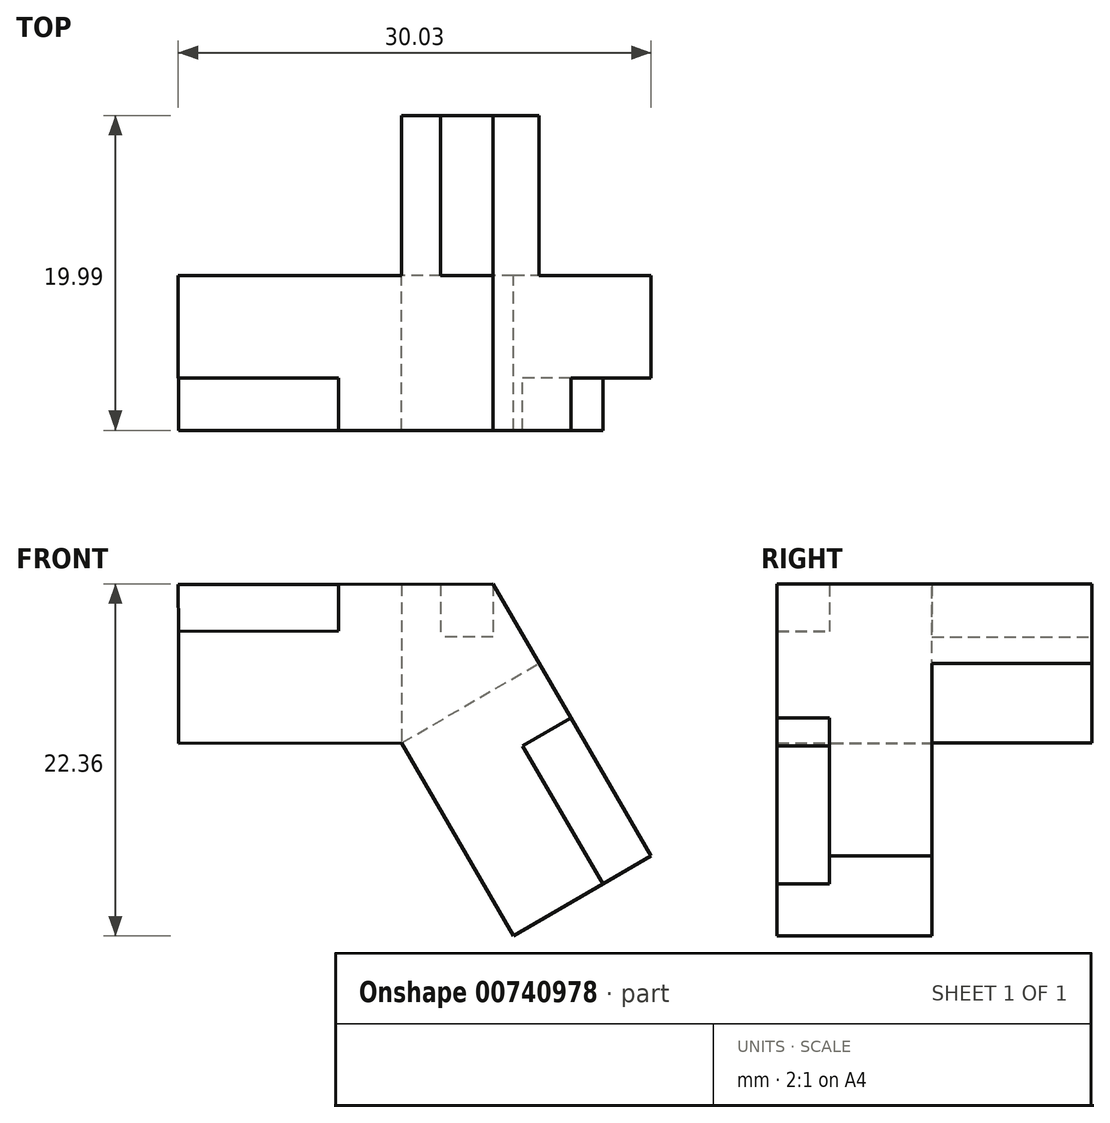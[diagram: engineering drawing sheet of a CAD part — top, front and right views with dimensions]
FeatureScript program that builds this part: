
annotation { "Feature Type Name" : "Feature", "Feature Type Description" : "" }
export const myFeature = defineFeature(function(context is Context, id is Id, definition is map)
    precondition{}
    {
        {
            var Q0;
            Q0=qCreatedBy(makeId("Front.planeOp"),FACE);
            var sketch = newSketch(context, id + "F0", { "sketchPlane" : qUnion([Q0])});
            skLineSegment(sketch, "E0.0", {"start": v(14.19, 24.71) * mm, "end": v(21.3, 12.46) * mm});
            skLineSegment(sketch, "E0.5", {"start": v(0.02, 24.68) * mm, "end": v(14.19, 24.71) * mm});
            skPoint(sketch, "E0.0.midPoint", {"position": v(21.3, 12.46) * mm});
            skLineSegment(sketch, "E1.0", {"start": v(19.99, 34.82) * mm, "end": v(30.03, 17.53) * mm});
            skLineSegment(sketch, "E1.5", {"start": v(0, 34.77) * mm, "end": v(19.99, 34.82) * mm});
            skPoint(sketch, "E1.0.midPoint", {"position": v(30.03, 17.53) * mm});
            skLineSegment(sketch, "E2", {"start": v(0, 34.77) * mm, "end": v(0.02, 24.68) * mm});
            skLineSegment(sketch, "E3", {"start": v(21.3, 12.46) * mm, "end": v(30.03, 17.53) * mm});
            skPoint(sketch, "E4.orphan", {"position": v(28.41, 0.21) * mm});
            skPoint(sketch, "E5.orphan", {"position": v(40.06, 0.24) * mm});
            skSolve(sketch);
        }
        {
            var Q0;
            Q0 = qSketchRegion(id + "F0", true);
            extrude(context, id + "F1", {"entities" : qUnion([Q0]), "depth" : 19.99 * mm, "offsetDistance" : 25.4 * mm});
        }
        {
            var Q0;
            Q0=makeQuery(id+"F1.opExtrude","CAP_FACE",FACE,{"disambiguationData":[OSD([sQuery(id+"F0.wireOp",EDGE,"E0.0"),sQuery(id+"F0.wireOp",EDGE,"E0.5"),sQuery(id+"F0.wireOp",EDGE,"E1.0"),sQuery(id+"F0.wireOp",EDGE,"E1.5"),sQuery(id+"F0.wireOp",EDGE,"E2"),sQuery(id+"F0.wireOp",EDGE,"E3")])],"isStart":true});
            var sketch = newSketch(context, id + "F2", { "sketchPlane" : qUnion([Q0])});
            skLineSegment(sketch, "E6.bottom", {"start": v(-19.99, 34.82) * mm, "end": v(-16.66, 34.82) * mm});
            skLineSegment(sketch, "E6.top", {"start": v(-19.99, 31.46) * mm, "end": v(-16.66, 31.46) * mm});
            skLineSegment(sketch, "E6.left", {"start": v(-19.99, 34.82) * mm, "end": v(-19.99, 31.46) * mm});
            skLineSegment(sketch, "E6.right", {"start": v(-16.66, 34.82) * mm, "end": v(-16.66, 31.46) * mm});
            skSolve(sketch);
        }
        {
            var Q0;
            Q0 = qSketchRegion(id + "F2", true);
            extrude(context, id + "F3", {"entities" : qUnion([Q0]), "operationType" : NewBodyOperationType.REMOVE, "oppositeDirection" : true, "depth" : 10.16 * mm, "offsetDistance" : 25.4 * mm});
        }
        {
            var Q0;
            Q0=makeQuery(id+"F1.opExtrude","SWEPT_FACE",FACE,{"disambiguationData":[OSD([sQuery(id+"F0.wireOp",EDGE,"E2")])]});
            var sketch = newSketch(context, id + "F4", { "sketchPlane" : qUnion([Q0])});
            skLineSegment(sketch, "E7.bottom", {"start": v(19.99, 34.77) * mm, "end": v(16.66, 34.77) * mm});
            skLineSegment(sketch, "E7.top", {"start": v(19.99, 31.8) * mm, "end": v(16.66, 31.8) * mm});
            skLineSegment(sketch, "E7.left", {"start": v(19.99, 34.77) * mm, "end": v(19.99, 31.8) * mm});
            skLineSegment(sketch, "E7.right", {"start": v(16.66, 34.77) * mm, "end": v(16.66, 31.8) * mm});
            skSolve(sketch);
        }
        {
            var Q0;
            Q0 = qSketchRegion(id + "F4", true);
            extrude(context, id + "F5", {"entities" : qUnion([Q0]), "operationType" : NewBodyOperationType.REMOVE, "oppositeDirection" : true, "depth" : 10.16 * mm, "offsetDistance" : 25.4 * mm});
        }
        {
            var Q0;
            Q0=makeQuery(id+"F1.opExtrude","SWEPT_FACE",FACE,{"disambiguationData":[OSD([sQuery(id+"F0.wireOp",EDGE,"E3")])]});
            var sketch = newSketch(context, id + "F6", { "sketchPlane" : qUnion([Q0])});
            skLineSegment(sketch, "E8.bottom", {"start": v(34.77, 19.99) * mm, "end": v(31.22, 19.99) * mm});
            skLineSegment(sketch, "E8.top", {"start": v(34.77, 16.66) * mm, "end": v(31.22, 16.66) * mm});
            skLineSegment(sketch, "E8.left", {"start": v(34.77, 19.99) * mm, "end": v(34.77, 16.66) * mm});
            skLineSegment(sketch, "E8.right", {"start": v(31.22, 19.99) * mm, "end": v(31.22, 16.66) * mm});
            skSolve(sketch);
        }
        {
            var Q0;
            Q0 = qSketchRegion(id + "F6", true);
            extrude(context, id + "F7", {"entities" : qUnion([Q0]), "operationType" : NewBodyOperationType.REMOVE, "oppositeDirection" : true, "depth" : 10.16 * mm, "offsetDistance" : 25.4 * mm});
        }
        {
            var Q0;
            Q0=makeQuery(id+"F1.opExtrude","CAP_FACE",FACE,{"disambiguationData":[OSD([sQuery(id+"F0.wireOp",EDGE,"E0.0"),sQuery(id+"F0.wireOp",EDGE,"E0.5"),sQuery(id+"F0.wireOp",EDGE,"E1.0"),sQuery(id+"F0.wireOp",EDGE,"E1.5"),sQuery(id+"F0.wireOp",EDGE,"E2"),sQuery(id+"F0.wireOp",EDGE,"E3")])],"isStart":true});
            var sketch = newSketch(context, id + "F8", { "sketchPlane" : qUnion([Q0])});
            skLineSegment(sketch, "E9.bottom", {"start": v(-14.19, 38.06) * mm, "end": v(0, 38.06) * mm});
            skLineSegment(sketch, "E9.top", {"start": v(-14.19, 19.42) * mm, "end": v(0, 19.42) * mm});
            skLineSegment(sketch, "E9.left", {"start": v(-14.19, 38.06) * mm, "end": v(-14.19, 19.42) * mm});
            skLineSegment(sketch, "E9.right", {"start": v(0, 38.06) * mm, "end": v(0, 19.42) * mm});
            skSolve(sketch);
        }
        {
            var Q0;
            Q0 = qSketchRegion(id + "F8", true);
            extrude(context, id + "F9", {"entities" : qUnion([Q0]), "operationType" : NewBodyOperationType.REMOVE, "oppositeDirection" : true, "depth" : 10.16 * mm, "offsetDistance" : 25.4 * mm});
        }
        {
            var Q0;
            Q0=makeQuery(id+"F1.opExtrude","CAP_FACE",FACE,{"disambiguationData":[OSD([sQuery(id+"F0.wireOp",EDGE,"E0.0"),sQuery(id+"F0.wireOp",EDGE,"E0.5"),sQuery(id+"F0.wireOp",EDGE,"E1.0"),sQuery(id+"F0.wireOp",EDGE,"E1.5"),sQuery(id+"F0.wireOp",EDGE,"E2"),sQuery(id+"F0.wireOp",EDGE,"E3")])],"isStart":true});
            var sketch = newSketch(context, id + "F10", { "sketchPlane" : qUnion([Q0])});
            skLineSegment(sketch, "E10", {"start": v(-14.19, 24.71) * mm, "end": v(-28.65, 33.1) * mm});
            skLineSegment(sketch, "E11", {"start": v(-28.65, 33.1) * mm, "end": v(-36.88, 18.93) * mm});
            skLineSegment(sketch, "E12", {"start": v(-36.88, 18.93) * mm, "end": v(-16.66, 7.2) * mm});
            skLineSegment(sketch, "E13", {"start": v(-16.66, 7.2) * mm, "end": v(-8.52, 21.21) * mm});
            skLineSegment(sketch, "E14", {"start": v(-8.52, 21.21) * mm, "end": v(-14.19, 24.71) * mm});
            skSolve(sketch);
        }
        {
            var Q0;
            Q0 = qSketchRegion(id + "F10", true);
            extrude(context, id + "F11", {"entities" : qUnion([Q0]), "operationType" : NewBodyOperationType.REMOVE, "oppositeDirection" : true, "depth" : 10.16 * mm, "offsetDistance" : 25.4 * mm});
        }
    });
